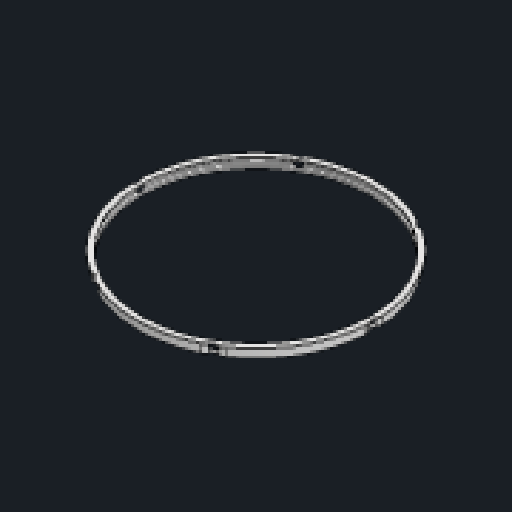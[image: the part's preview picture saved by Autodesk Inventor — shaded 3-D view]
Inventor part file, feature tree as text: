
AUTODESK INVENTOR PART (.ipt)
format: ipt  version: 2023.2 (Build 272271030, 271C)  size: 154,624 bytes
history: native  units: mm
features: sketch x3, extrude x2, revolve x1, fillet x1, pattern_circular x1
ambient origin geometry x8: Origin, YZ Plane, XZ Plane, XY Plane, X Axis, Y Axis, Z Axis, Center Point
bodies: Solid1 (feature_tree)
feature tree (8):
  revolve  "Revolution1"  [1 undecoded]
  extrude  "Extrusion1"  Depth=2.5mm
  extrude  "Extrusion2"  Depth=67.0mm
  fillet  "Fillet1"  Radius=3.5mm
  pattern_circular  "Circular Pattern1"  [2 undecoded]
  sketch  "Sketch1"  dims[d0=5.0mm d1=69.0mm]
  sketch  "Sketch2"  dims[d4=1.0mm d5=2.5mm]
  sketch  "Sketch3"  dims[d6=67.5mm d7=67.0mm d9=3.5mm d11=2.0mm d12=6.0mm d13=0.5mm d15=360.0deg d16=5.1mm d17=72.25mm d18=10.0mm d19=0.0mm d20=8.0mm d21=10.0mm d22=0.0mm d23=4.0mm d24=60.0mm d25=360.0deg d27=0.5mm d28=1.0mm]
note: 3 required parameter values undecoded (feature->parameter linkage not recoverable at this tier; creation-order binding heuristic only, values carry confidence <= 0.55)